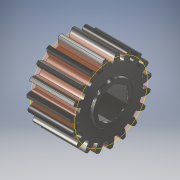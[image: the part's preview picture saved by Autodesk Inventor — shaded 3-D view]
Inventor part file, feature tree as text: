
AUTODESK INVENTOR PART (.ipt)
format: ipt  version: 2018 (Build 220112000, 112)  size: 243,712 bytes
history: native  units: in
note: dims shown in document units (in); Inventor stores cm internally (conversion verified against a paired STEP export)
features: other x2, sketch x1, extrude x1
ambient origin geometry x8: Origin, YZ Plane, XZ Plane, XY Plane, X Axis, Y Axis, Z Axis, Center Point
bodies: Solid1 (feature_tree)
feature tree (4):
  sketch  "Sketch1"  dims[d0=0.95in d1=1.0in d2=0.0in]
  other  "Srf1"
  other  "Cut-Extrude1"
  extrude  "ExtrusionSrf1"  Depth=1.0in TaperAngle=0.0deg
